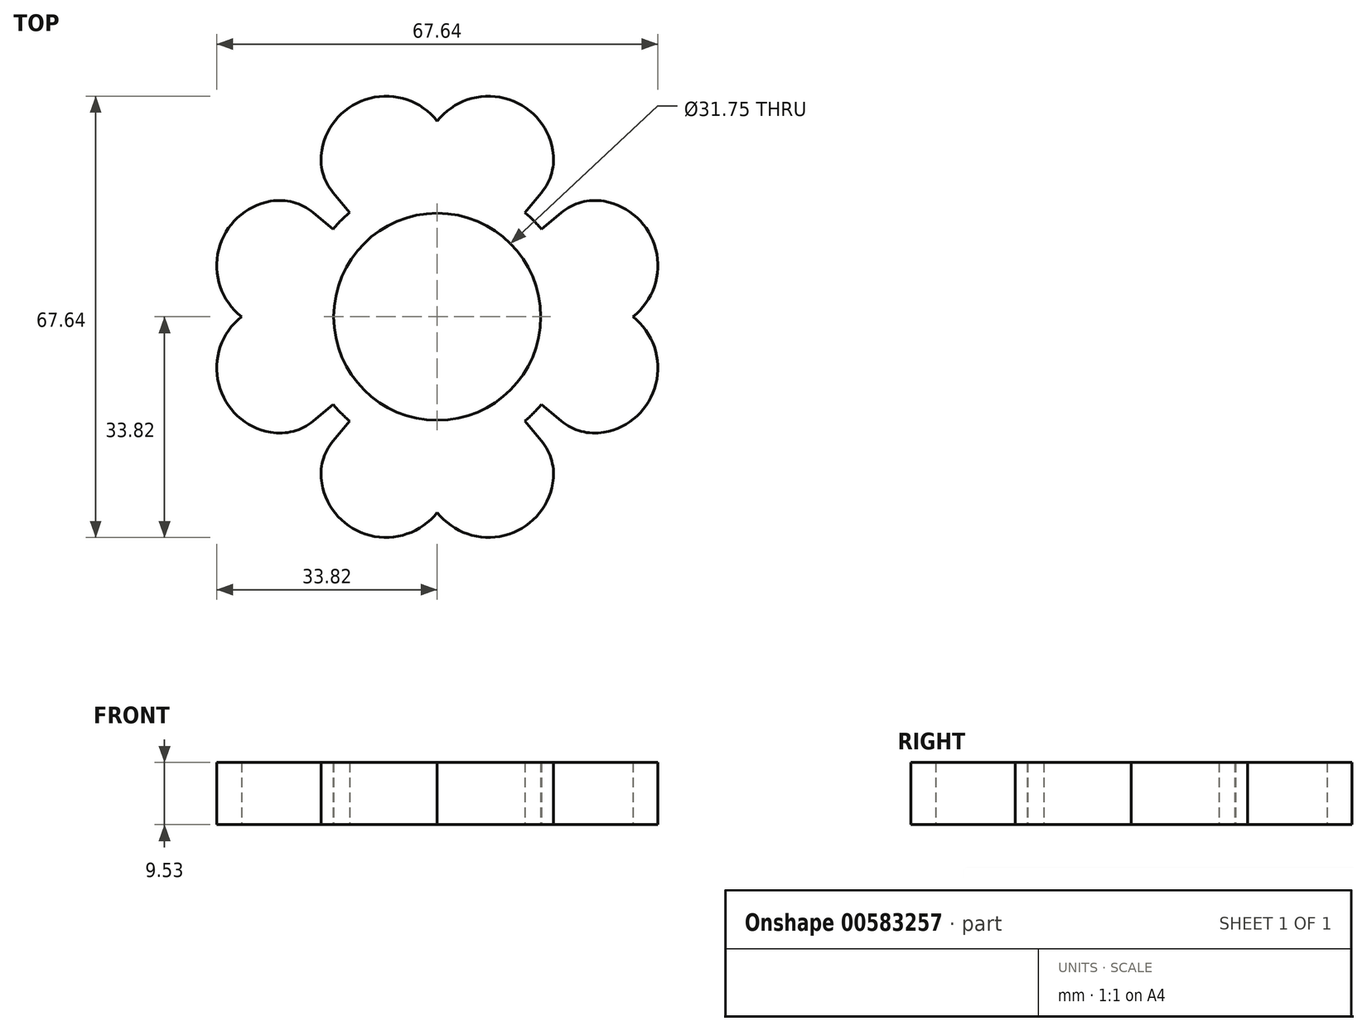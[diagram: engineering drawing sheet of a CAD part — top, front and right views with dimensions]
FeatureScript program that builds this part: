
annotation { "Feature Type Name" : "Feature", "Feature Type Description" : "" }
export const myFeature = defineFeature(function(context is Context, id is Id, definition is map)
    precondition{}
    {
        {
            var Q0;
            Q0=qCreatedBy(makeId("Top.planeOp"),FACE);
            var sketch = newSketch(context, id + "F0", { "sketchPlane" : qUnion([Q0])});
            skCircle(sketch, "E0", {"center": v(0, 0) * mm, "radius": 15.88 * mm});
            skArc(sketch, "E1.0", {"start": v(-13.42, 16) * mm, "mid": v(-20.88, 0) * mm, "end": v(-13.42, -16) * mm});
            skLineSegment(sketch, "E2", {"start": v(0, 0) * mm, "end": v(0, 30) * mm, "construction": true});
            skLineSegment(sketch, "E3", {"start": v(13.42, 16) * mm, "end": v(17.36, 20.68) * mm});
            skArc(sketch, "E4", {"start": v(17.36, 20.68) * mm, "mid": v(12.59, 32.63) * mm, "end": v(0, 30) * mm});
            skLineSegment(sketch, "E5.MirrorCS", {"start": v(-13.42, 16) * mm, "end": v(-17.36, 20.68) * mm});
            skArc(sketch, "E6.MirrorCS", {"start": v(-17.36, 20.68) * mm, "mid": v(-12.59, 32.63) * mm, "end": v(0, 30) * mm});
            skLineSegment(sketch, "E7.1.0", {"start": v(-16, -13.42) * mm, "end": v(-20.68, -17.36) * mm});
            skArc(sketch, "E7.1.1", {"start": v(-20.68, -17.36) * mm, "mid": v(-32.63, -12.59) * mm, "end": v(-30, 0) * mm});
            skArc(sketch, "E7.1.2", {"start": v(-20.68, 17.36) * mm, "mid": v(-32.63, 12.59) * mm, "end": v(-30, 0) * mm});
            skLineSegment(sketch, "E7.1.3", {"start": v(-16, 13.42) * mm, "end": v(-20.68, 17.36) * mm});
            skLineSegment(sketch, "E7.2.0", {"start": v(13.42, -16) * mm, "end": v(17.36, -20.68) * mm});
            skArc(sketch, "E7.2.1", {"start": v(17.36, -20.68) * mm, "mid": v(12.59, -32.63) * mm, "end": v(0, -30) * mm});
            skArc(sketch, "E7.2.2", {"start": v(-17.36, -20.68) * mm, "mid": v(-12.59, -32.63) * mm, "end": v(0, -30) * mm});
            skLineSegment(sketch, "E7.2.3", {"start": v(-13.42, -16) * mm, "end": v(-17.36, -20.68) * mm});
            skLineSegment(sketch, "E7.3.0", {"start": v(16, 13.42) * mm, "end": v(20.68, 17.36) * mm});
            skArc(sketch, "E7.3.1", {"start": v(20.68, 17.36) * mm, "mid": v(32.63, 12.59) * mm, "end": v(30, 0) * mm});
            skArc(sketch, "E7.3.2", {"start": v(20.68, -17.36) * mm, "mid": v(32.63, -12.59) * mm, "end": v(30, 0) * mm});
            skLineSegment(sketch, "E7.3.3", {"start": v(16, -13.42) * mm, "end": v(20.68, -17.36) * mm});
            skArc(sketch, "E8.trimOffspring", {"start": v(16, 13.42) * mm, "mid": v(14.76, 14.76) * mm, "end": v(13.42, 16) * mm});
            skArc(sketch, "E9.trimOffspring", {"start": v(13.42, -16) * mm, "mid": v(14.76, -14.76) * mm, "end": v(16, -13.42) * mm});
            skSolve(sketch);
        }
        {
            var Q0;
            {var subQ0=sQuery(id+"F0.wireOp",EDGE,"E7.1.0");Q0=makeQuery(id+"F0.imprint","IMPRINT",FACE,{"disambiguationData":[TD([[makeQuery(id+"F0.imprint","IMPRINT",EDGE,{"derivedFrom":subQ0}),-1.0]])]});}
            var Q1;
            Q1=makeQuery(id+"F0.imprint","IMPRINT",FACE,{"disambiguationData":[TD([[makeQuery(id+"F0.imprint","IMPRINT",EDGE,{"derivedFrom":sQuery(id+"F0.wireOp",EDGE,"E0")}),-1.0]])]});
            extrude(context, id + "F1", {"entities" : qUnion([Q0, Q1]), "depth" : 9.52 * mm, "offsetDistance" : 25 * mm});
        }
        {
            var Q0;
            Q0=makeQuery(id+"F1.opExtrude","SWEPT_EDGE",EDGE,{"disambiguationData":[OSD([sQuery(id+"F0.wireOp",EDGE,"E7.1.0"),sQuery(id+"F0.wireOp",EDGE,"E7.1.1")])]});
            var Q1;
            Q1=makeQuery(id+"F1.opExtrude","SWEPT_EDGE",EDGE,{"disambiguationData":[OSD([sQuery(id+"F0.wireOp",EDGE,"E7.3.2"),sQuery(id+"F0.wireOp",EDGE,"E7.3.3")])]});
            var Q2;
            Q2=makeQuery(id+"F1.opExtrude","SWEPT_EDGE",EDGE,{"disambiguationData":[OSD([sQuery(id+"F0.wireOp",EDGE,"E3"),sQuery(id+"F0.wireOp",EDGE,"E4")])]});
            var Q3;
            Q3=makeQuery(id+"F1.opExtrude","SWEPT_EDGE",EDGE,{"disambiguationData":[OSD([sQuery(id+"F0.wireOp",EDGE,"E7.3.0"),sQuery(id+"F0.wireOp",EDGE,"E7.3.1")])]});
            var Q4;
            Q4=makeQuery(id+"F1.opExtrude","SWEPT_EDGE",EDGE,{"disambiguationData":[OSD([sQuery(id+"F0.wireOp",EDGE,"E7.2.2"),sQuery(id+"F0.wireOp",EDGE,"E7.2.3")])]});
            var Q5;
            Q5=makeQuery(id+"F1.opExtrude","SWEPT_EDGE",EDGE,{"disambiguationData":[OSD([sQuery(id+"F0.wireOp",EDGE,"E7.1.2"),sQuery(id+"F0.wireOp",EDGE,"E7.1.3")])]});
            var Q6;
            Q6=makeQuery(id+"F1.opExtrude","SWEPT_EDGE",EDGE,{"disambiguationData":[OSD([sQuery(id+"F0.wireOp",EDGE,"E5.MirrorCS"),sQuery(id+"F0.wireOp",EDGE,"E6.MirrorCS")])]});
            var Q7;
            Q7=makeQuery(id+"F1.opExtrude","SWEPT_EDGE",EDGE,{"disambiguationData":[OSD([sQuery(id+"F0.wireOp",EDGE,"E7.2.0"),sQuery(id+"F0.wireOp",EDGE,"E7.2.1")])]});
            fillet(context, id + "F2", {"entities" : qUnion([Q0, Q1, Q2, Q3, Q4, Q5, Q6, Q7]), "radius" : 8 * mm, "tangentPropagation" : true, "allowEdgeOverflow" : false});
        }
    });
